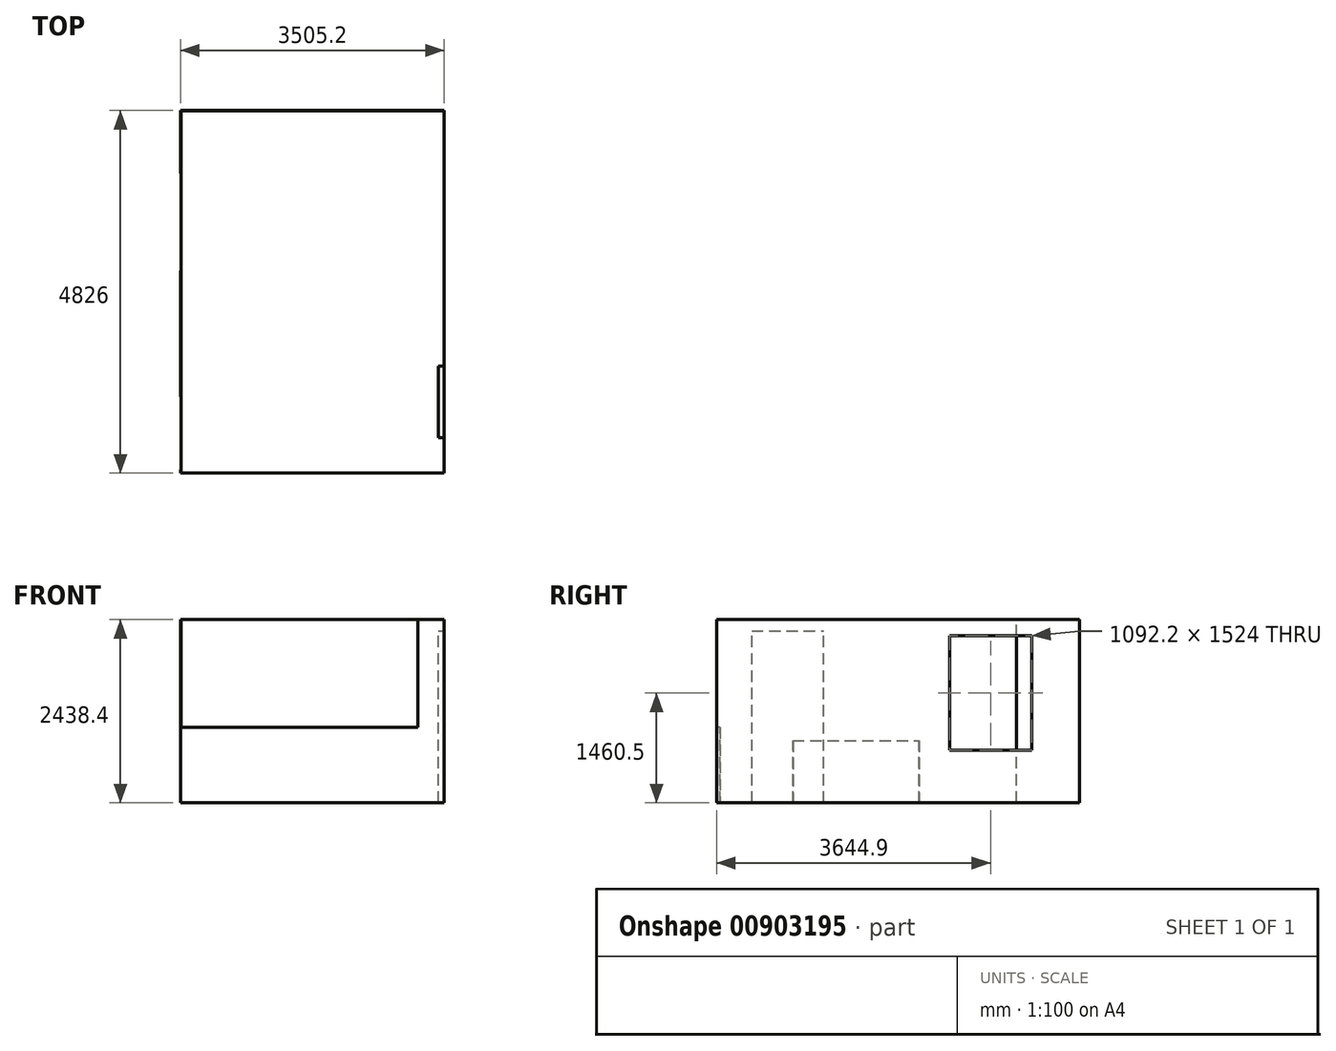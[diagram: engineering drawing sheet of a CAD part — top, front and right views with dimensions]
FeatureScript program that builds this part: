
annotation { "Feature Type Name" : "Feature", "Feature Type Description" : "" }
export const myFeature = defineFeature(function(context is Context, id is Id, definition is map)
    precondition{}
    {
        {
            var Q0;
            Q0=qCreatedBy(makeId("Top.planeOp"),FACE);
            var sketch = newSketch(context, id + "F0", { "sketchPlane" : qUnion([Q0])});
            skLineSegment(sketch, "E0.bottom", {"start": v(-3456.48, 4779.03) * mm, "end": v(48.72, 4779.03) * mm});
            skLineSegment(sketch, "E0.top", {"start": v(-3456.48, -46.97) * mm, "end": v(48.72, -46.97) * mm});
            skLineSegment(sketch, "E0.left", {"start": v(-3456.48, 4779.03) * mm, "end": v(-3456.48, -46.97) * mm});
            skLineSegment(sketch, "E0.right", {"start": v(48.72, 4779.03) * mm, "end": v(48.72, -46.97) * mm});
            skSolve(sketch);
        }
        {
            var Q0;
            Q0=makeQuery(id+"F0.imprint","IMPRINT",FACE,{"disambiguationData":[TD([[makeQuery(id+"F0.imprint","IMPRINT",EDGE,{"derivedFrom":sQuery(id+"F0.wireOp",EDGE,"E0.bottom")}),-1.0]])]});
            extrude(context, id + "F1", {"entities" : qUnion([Q0]), "depth" : 2438.4 * mm, "offsetDistance" : 25.4 * mm});
        }
        {
            var Q0;
            Q0=makeQuery(id+"F1.opExtrude","CAP_FACE",FACE,{"disambiguationData":[OSD([sQuery(id+"F0.wireOp",EDGE,"E0.bottom"),sQuery(id+"F0.wireOp",EDGE,"E0.top"),sQuery(id+"F0.wireOp",EDGE,"E0.left"),sQuery(id+"F0.wireOp",EDGE,"E0.right")])],"isStart":false});
            shell(context, id + "F2", {"entities" : qUnion([Q0]), "thickness" : 2.54 * mm});
        }
        {
            var Q0;
            Q0=makeQuery(id+"F1.opExtrude","SWEPT_FACE",FACE,{"disambiguationData":[OSD([sQuery(id+"F0.wireOp",EDGE,"E0.left")])]});
            var sketch = newSketch(context, id + "F3", { "sketchPlane" : qUnion([Q0])});
            skLineSegment(sketch, "E1.bottom", {"start": v(-3940.83, 2438.4) * mm, "end": v(-2645.43, 2438.4) * mm});
            skLineSegment(sketch, "E1.top", {"start": v(-3940.83, 0) * mm, "end": v(-2645.43, 0) * mm});
            skLineSegment(sketch, "E1.left", {"start": v(-3940.83, 2438.4) * mm, "end": v(-3940.83, 0) * mm});
            skLineSegment(sketch, "E1.right", {"start": v(-2645.43, 2438.4) * mm, "end": v(-2645.43, 0) * mm});
            skLineSegment(sketch, "E2.bottom", {"start": v(-969.03, 2438.4) * mm, "end": v(0, 2438.4) * mm});
            skLineSegment(sketch, "E2.top", {"start": v(-969.03, 0) * mm, "end": v(0, 0) * mm});
            skLineSegment(sketch, "E2.left", {"start": v(-969.03, 2438.4) * mm, "end": v(-969.03, 0) * mm});
            skLineSegment(sketch, "E2.right", {"start": v(0, 2438.4) * mm, "end": v(0, 0) * mm});
            skSolve(sketch);
        }
        {
            var Q0;
            Q0=makeQuery(id+"F3.imprint","IMPRINT",FACE,{"disambiguationData":[TD([[makeQuery(id+"F3.imprint","IMPRINT",EDGE,{"derivedFrom":sQuery(id+"F3.wireOp",EDGE,"E1.bottom")}),-1.0]])]});
            var Q1;
            Q1=makeQuery(id+"F3.imprint","IMPRINT",FACE,{"disambiguationData":[TD([[makeQuery(id+"F3.imprint","IMPRINT",EDGE,{"derivedFrom":sQuery(id+"F3.wireOp",EDGE,"E2.bottom")}),-1.0]])]});
            extrude(context, id + "F4", {"entities" : qUnion([Q0, Q1]), "operationType" : NewBodyOperationType.REMOVE, "oppositeDirection" : true, "depth" : 5.08 * mm, "offsetDistance" : 25.4 * mm});
        }
        {
            var Q0;
            Q0=makeQuery(id+"F1.opExtrude","SWEPT_FACE",FACE,{"disambiguationData":[OSD([sQuery(id+"F0.wireOp",EDGE,"E0.right")])]});
            var sketch = newSketch(context, id + "F5", { "sketchPlane" : qUnion([Q0])});
            skLineSegment(sketch, "E3.bottom", {"start": v(3051.83, 2222.5) * mm, "end": v(4144.03, 2222.5) * mm});
            skLineSegment(sketch, "E3.top", {"start": v(3051.83, 698.5) * mm, "end": v(4144.03, 698.5) * mm});
            skLineSegment(sketch, "E3.left", {"start": v(3051.83, 2222.5) * mm, "end": v(3051.83, 698.5) * mm});
            skLineSegment(sketch, "E3.right", {"start": v(4144.03, 2222.5) * mm, "end": v(4144.03, 698.5) * mm});
            skSolve(sketch);
        }
        {
            var Q0;
            Q0=makeQuery(id+"F5.imprint","IMPRINT",FACE,{"disambiguationData":[TD([[makeQuery(id+"F5.imprint","IMPRINT",EDGE,{"derivedFrom":sQuery(id+"F5.wireOp",EDGE,"E3.bottom")}),-1.0]])]});
            extrude(context, id + "F6", {"entities" : qUnion([Q0]), "operationType" : NewBodyOperationType.REMOVE, "oppositeDirection" : true, "depth" : 25.4 * mm, "offsetDistance" : 25.4 * mm});
        }
        {
            var Q0;
            Q0=makeQuery(id+"F2.opShell","OFFSET_FACE",FACE,{"disambiguationData":[OSD([sQuery(id+"F0.wireOp",EDGE,"E0.right")])]});
            var sketch = newSketch(context, id + "F7", { "sketchPlane" : qUnion([Q0])});
            skLineSegment(sketch, "E4.bottom", {"start": v(-422.93, 0) * mm, "end": v(-1375.43, 0) * mm});
            skLineSegment(sketch, "E4.top", {"start": v(-422.93, 2286) * mm, "end": v(-1375.43, 2286) * mm});
            skLineSegment(sketch, "E4.left", {"start": v(-422.93, 0) * mm, "end": v(-422.93, 2286) * mm});
            skLineSegment(sketch, "E4.right", {"start": v(-1375.43, 0) * mm, "end": v(-1375.43, 2286) * mm});
            skSolve(sketch);
        }
        {
            var Q0;
            Q0 = qSketchRegion(id + "F7", true);
            extrude(context, id + "F8", {"entities" : qUnion([Q0]), "operationType" : NewBodyOperationType.ADD, "depth" : 76.2 * mm, "offsetDistance" : 25.4 * mm});
        }
        {
            var Q0;
            Q0=qCreatedBy(makeId("Top.planeOp"),FACE);
            cPlane(context, id + "F9", {"entities" : qUnion([Q0]), "cplaneType" : CPlaneType.OFFSET, "offset" : 1727.2 * mm, "width" : 152.4 * mm, "height" : 152.4 * mm});
        }
        {
            var Q0;
            Q0=qCreatedBy(id+"F9.planeOp",FACE);
            var sketch = newSketch(context, id + "F10", { "sketchPlane" : qUnion([Q0])});
            skCircle(sketch, "E5", {"center": v(-3387.94, -986.37) * mm, "radius": 279.4 * mm});
            skSolve(sketch);
        }
        {
            var Q0;
            Q0 = qSketchRegion(id + "F10", true);
            extrude(context, id + "F11", {"entities" : qUnion([Q0]), "oppositeDirection" : true, "depth" : 304.8 * mm, "offsetDistance" : 25.4 * mm});
        }
        {
            var Q0;
            Q0=makeQuery(id+"F11.opExtrude","SWEPT_BODY",BODY,{"disambiguationData":[OSD([sQuery(id+"F10.wireOp",EDGE,"E5")])]});
            deleteBodies(context, id + "F12", {"entities" : qUnion([Q0])});
        }
        {
            var Q0;
            {var subQ1=sQuery(id+"F0.wireOp",EDGE,"E0.left");Q0=makeQuery(id+"F4.boolean.opBoolean","SPLIT",FACE,{"disambiguationData":[TD([makeQuery(id+"F4.opExtrude","SWEPT_FACE",FACE,{"disambiguationData":[OSD([sQuery(id+"F3.wireOp",EDGE,"E1.right")])]})])],"derivedFrom":makeQuery(id+"F2.opShell","OFFSET_FACE",FACE,{"disambiguationData":[OSD([subQ1])]})});}
            var sketch = newSketch(context, id + "F13", { "sketchPlane" : qUnion([Q0])});
            skLineSegment(sketch, "E6.bottom", {"start": v(969.03, 2438.4) * mm, "end": v(2645.43, 2438.4) * mm});
            skLineSegment(sketch, "E6.top", {"start": v(969.03, 828.58) * mm, "end": v(2645.43, 828.58) * mm});
            skLineSegment(sketch, "E6.left", {"start": v(969.03, 2438.4) * mm, "end": v(969.03, 828.58) * mm});
            skLineSegment(sketch, "E6.right", {"start": v(2645.43, 2438.4) * mm, "end": v(2645.43, 828.58) * mm});
            skSolve(sketch);
        }
        {
            var Q0;
            Q0=makeQuery(id+"F13.imprint","IMPRINT",FACE,{"disambiguationData":[TD([[makeQuery(id+"F13.imprint","IMPRINT",EDGE,{"derivedFrom":sQuery(id+"F13.wireOp",EDGE,"E6.bottom")}),1.0]])]});
            extrude(context, id + "F14", {"entities" : qUnion([Q0]), "operationType" : NewBodyOperationType.REMOVE, "oppositeDirection" : true, "depth" : 25.4 * mm, "offsetDistance" : 25.4 * mm});
        }
        {
            var Q0;
            Q0=makeQuery(id+"F1.opExtrude","SWEPT_FACE",FACE,{"disambiguationData":[OSD([sQuery(id+"F0.wireOp",EDGE,"E0.top")])]});
            var sketch = newSketch(context, id + "F15", { "sketchPlane" : qUnion([Q0])});
            skLineSegment(sketch, "E7.bottom", {"start": v(-298.69, 2438.4) * mm, "end": v(-4252.37, 2438.4) * mm});
            skLineSegment(sketch, "E7.top", {"start": v(-298.69, 1005.88) * mm, "end": v(-4252.37, 1005.88) * mm});
            skLineSegment(sketch, "E7.left", {"start": v(-298.69, 2438.4) * mm, "end": v(-298.69, 1005.88) * mm});
            skLineSegment(sketch, "E7.right", {"start": v(-4252.37, 2438.4) * mm, "end": v(-4252.37, 1005.88) * mm});
            skSolve(sketch);
        }
        {
            var Q0;
            Q0 = qSketchRegion(id + "F15", true);
            extrude(context, id + "F16", {"entities" : qUnion([Q0]), "operationType" : NewBodyOperationType.REMOVE, "oppositeDirection" : true, "depth" : 127 * mm, "offsetDistance" : 25.4 * mm});
        }
    });
